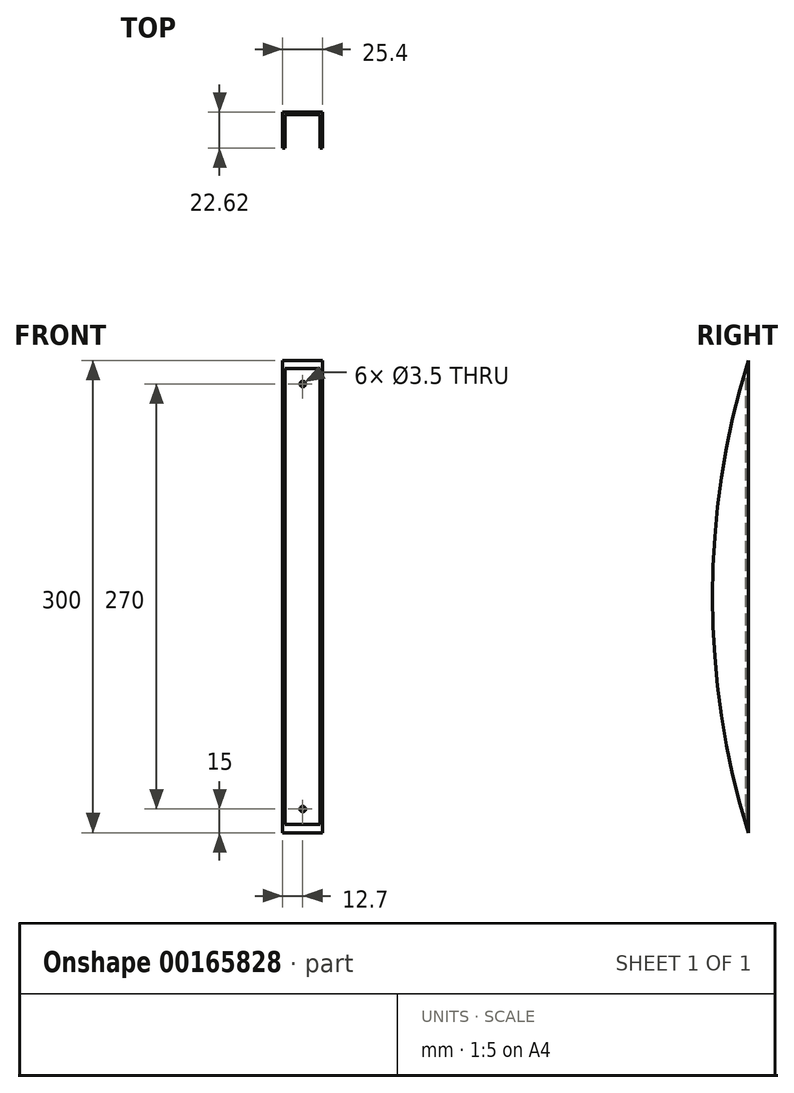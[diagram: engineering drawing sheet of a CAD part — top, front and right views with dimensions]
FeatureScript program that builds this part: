
annotation { "Feature Type Name" : "Feature", "Feature Type Description" : "" }
export const myFeature = defineFeature(function(context is Context, id is Id, definition is map)
    precondition{}
    {
        {
            var Q0;
            Q0=qCreatedBy(makeId("Right.planeOp"),FACE);
            var sketch = newSketch(context, id + "F0", { "sketchPlane" : qUnion([Q0])});
            skLineSegment(sketch, "E0.bottom", {"start": v(0, 0) * mm, "end": v(25.4, 0) * mm});
            skLineSegment(sketch, "E0.top", {"start": v(0, 300) * mm, "end": v(25.4, 300) * mm});
            skLineSegment(sketch, "E0.left", {"start": v(0, 0) * mm, "end": v(0, 300) * mm});
            skLineSegment(sketch, "E0.right", {"start": v(25.4, 0) * mm, "end": v(25.4, 300) * mm});
            skSolve(sketch);
        }
        {
            var Q0;
            Q0=qSketchRegion(id+"F0",true);
            extrude(context, id + "F1", {"entities" : qUnion([Q0]), "depth" : 25.4 * mm});
        }
        {
            var Q0;
            Q0=makeQuery(id+"F1.opExtrude","SWEPT_FACE",FACE,{"disambiguationData":[OSD([sQuery(id+"F0.wireOp",EDGE,"E0.top")])]});
            var sketch = newSketch(context, id + "F2", { "sketchPlane" : qUnion([Q0])});
            skLineSegment(sketch, "E1.0", {"start": v(1.59, 23.81) * mm, "end": v(1.59, 1.59) * mm});
            skLineSegment(sketch, "E1.1", {"start": v(23.81, 23.81) * mm, "end": v(1.59, 23.81) * mm});
            skLineSegment(sketch, "E1.2", {"start": v(23.81, 1.59) * mm, "end": v(23.81, 23.81) * mm});
            skLineSegment(sketch, "E1.3", {"start": v(1.59, 1.59) * mm, "end": v(23.81, 1.59) * mm});
            skSolve(sketch);
        }
        {
            var Q0;
            Q0=makeQuery(id+"F2.imprint","IMPRINT",FACE,{"disambiguationData":[TD([[makeQuery(id+"F2.imprint","IMPRINT",EDGE,{"derivedFrom":sQuery(id+"F2.wireOp",EDGE,"E1.0")}),1.0]])]});
            extrude(context, id + "F3", {"entities" : qUnion([Q0]), "operationType" : NewBodyOperationType.REMOVE, "oppositeDirection" : true, "depth" : 300 * mm});
        }
        {
            var Q0;
            Q0=makeQuery(id+"F1.opExtrude","CAP_FACE",FACE,{"disambiguationData":[OSD([sQuery(id+"F0.wireOp",EDGE,"E0.bottom"),sQuery(id+"F0.wireOp",EDGE,"E0.top"),sQuery(id+"F0.wireOp",EDGE,"E0.left"),sQuery(id+"F0.wireOp",EDGE,"E0.right")])],"isStart":false});
            var sketch = newSketch(context, id + "F4", { "sketchPlane" : qUnion([Q0])});
            skArc(sketch, "E2", {"start": v(25.4, 300) * mm, "mid": v(2.78, 150) * mm, "end": v(25.4, 0) * mm});
            skSolve(sketch);
        }
        {
            var Q0;
            Q0=makeQuery(id+"F4.imprint","IMPRINT",FACE,{"disambiguationData":[TD([[makeQuery(id+"F4.imprint","IMPRINT",EDGE,{"derivedFrom":sQuery(id+"F4.wireOp",EDGE,"E2")}),-1.0]])]});
            extrude(context, id + "F5", {"entities" : qUnion([Q0]), "operationType" : NewBodyOperationType.REMOVE, "oppositeDirection" : true, "depth" : 25.4 * mm});
        }
        {
            var Q0;
            Q0=makeQuery(id+"F1.opExtrude","SWEPT_FACE",FACE,{"disambiguationData":[OSD([sQuery(id+"F0.wireOp",EDGE,"E0.right")])]});
            var sketch = newSketch(context, id + "F6", { "sketchPlane" : qUnion([Q0])});
            skCircle(sketch, "E3", {"center": v(-12.7, 285) * mm, "radius": 1.75 * mm});
            skLineSegment(sketch, "E4", {"start": v(-12.7, 0) * mm, "end": v(-12.7, 300) * mm, "construction": true});
            skCircle(sketch, "E5", {"center": v(-12.7, 15) * mm, "radius": 1.75 * mm});
            skSolve(sketch);
        }
        {
            var Q0;
            Q0=qSketchRegion(id+"F6",true);
            extrude(context, id + "F7", {"entities" : qUnion([Q0]), "operationType" : NewBodyOperationType.REMOVE, "oppositeDirection" : true, "depth" : 25 * mm});
        }
    });
